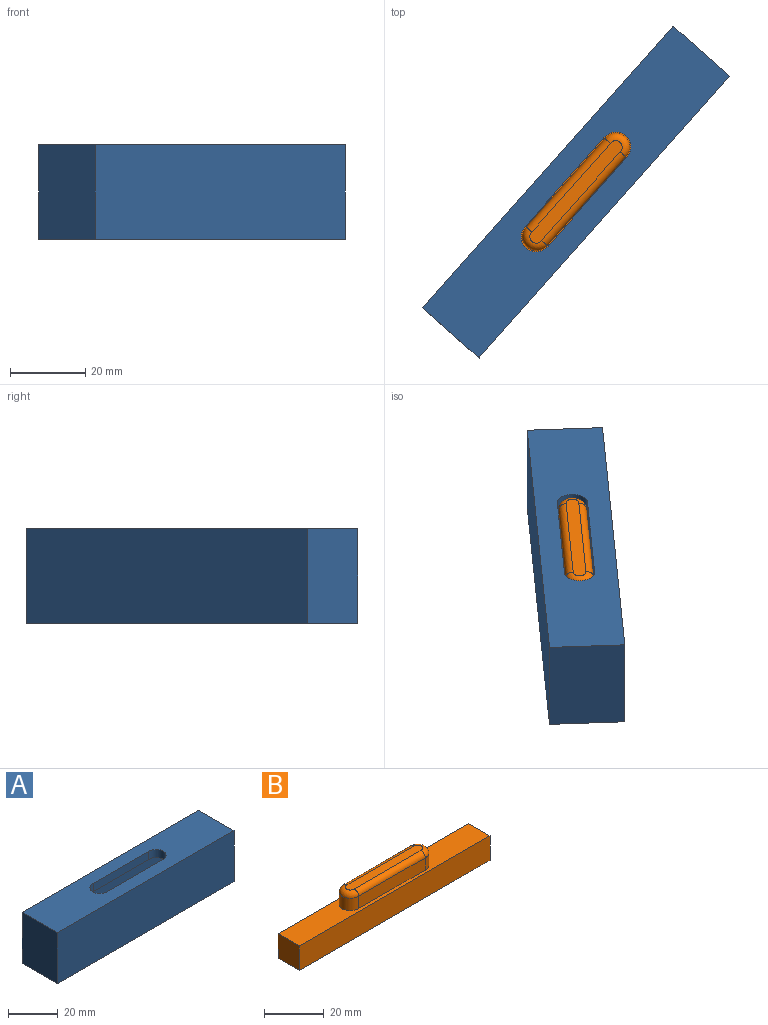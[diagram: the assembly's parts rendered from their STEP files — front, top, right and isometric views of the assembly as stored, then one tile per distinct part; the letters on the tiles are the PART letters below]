
ASSEMBLY  parts=2 mates=1
PART A: 15 faces, bbox 100x20x25 mm
  f0: plane 92x12mm, normal (0,0,-1), area 799.1mm2, adj f7,f8,f9,f10,f11,f12,f13,f14
  f1: plane 100x25mm, normal (0,1,0), area 2500mm2, adj f2,f4,f5,f6
  f2: plane 25x20mm, normal (-1,0,0), area 500mm2, adj f1,f3,f5,f6
  f3: plane 100x25mm, normal (0,-1,0), area 2500mm2, adj f2,f4,f5,f6
  f4: plane 25x20mm, normal (1,0,0), area 500mm2, adj f1,f3,f5,f6
  f5: plane 100x20mm, normal (0,0,1), area 1695.1mm2, adj f1,f2,f3,f4,f11,f12,f13,f14
  f6: plane 100x20mm, normal (0,0,-1), area 896mm2, adj f1,f2,f3,f4,f7,f8,f9,f10
  f7: plane 21x12mm, normal (1,0,0), area 252mm2, adj f0,f6,f8,f9
  f8: plane 92x21mm, normal (0,1,0), area 1932mm2, adj f0,f6,f7,f10
  f9: plane 92x21mm, normal (0,-1,0), area 1932mm2, adj f0,f6,f7,f10
  f10: plane 21x12mm, normal (-1,0,0), area 252mm2, adj f0,f6,f8,f9
  f11: cylinder r=4.01mm len=8.01mm, axis (0,0,1), area 52.1mm2, adj f0,f5,f12,f14
  f12: plane 31.37x4mm, normal (0,1,0), area 125.5mm2, adj f0,f5,f11,f13
  f13: cylinder r=4.01mm len=8.01mm, axis (0,0,1), area 52.1mm2, adj f0,f5,f12,f14
  f14: plane 31.37x4mm, normal (0,-1,0), area 125.5mm2, adj f0,f5,f11,f13
PART B: 15 faces, bbox 90x10x17 mm
  f0: plane 90x10mm, normal (0,1,0), area 900mm2, adj f1,f3,f4,f5
  f1: plane 10x10mm, normal (-1,0,0), area 100mm2, adj f0,f2,f4,f5
  f2: plane 90x10mm, normal (0,-1,0), area 900mm2, adj f1,f3,f4,f5
  f3: plane 10x10mm, normal (1,0,0), area 100mm2, adj f0,f2,f4,f5
  f4: plane 90x10mm, normal (0,0,1), area 621.5mm2, adj f0,f1,f2,f3,f6,f7,f8,f9
  f5: plane 90x10mm, normal (0,0,-1), area 900mm2, adj f0,f1,f2,f3
  f6: plane 31.39x5mm, normal (0,1,0), area 156.9mm2, adj f4,f7,f9,f11
  f7: cylinder r=3.71mm len=7.41mm, axis (0,0,-1), area 60.3mm2, adj f4,f6,f8,f13
  f8: plane 31.39x5mm, normal (0,-1,0), area 156.9mm2, adj f4,f7,f9,f14
  f9: cylinder r=3.71mm len=7.41mm, axis (0,0,-1), area 60.3mm2, adj f4,f6,f8,f12
  f10: plane 35.22x3.41mm, normal (0,0,1), area 117.3mm2, adj f11,f12,f13,f14
  f11: cylinder r=2mm len=31.52mm, axis (1,0,0), area 98.8mm2, adj f6,f10,f12,f13
  f12: torus R=1.71mm, axis (0,0,1), area 30.6mm2, adj f9,f10,f11,f14
  f13: torus R=1.71mm, axis (0,0,1), area 30.6mm2, adj f7,f10,f11,f14
  f14: cylinder r=2mm len=31.52mm, axis (-1,0,0), area 98.8mm2, adj f8,f10,f12,f13
PLACE A rot(axis=(0,0,-1),131.6deg) t=(20.81,-5.97,16.66)mm
PLACE B rot(axis=(0,0,-1),131.6deg) t=(20.81,-5.97,24.66)mm
MATE slider B.f10 <-> A.f5  axis (0,0,1) through (20.81,-5.97,41.66)mm
